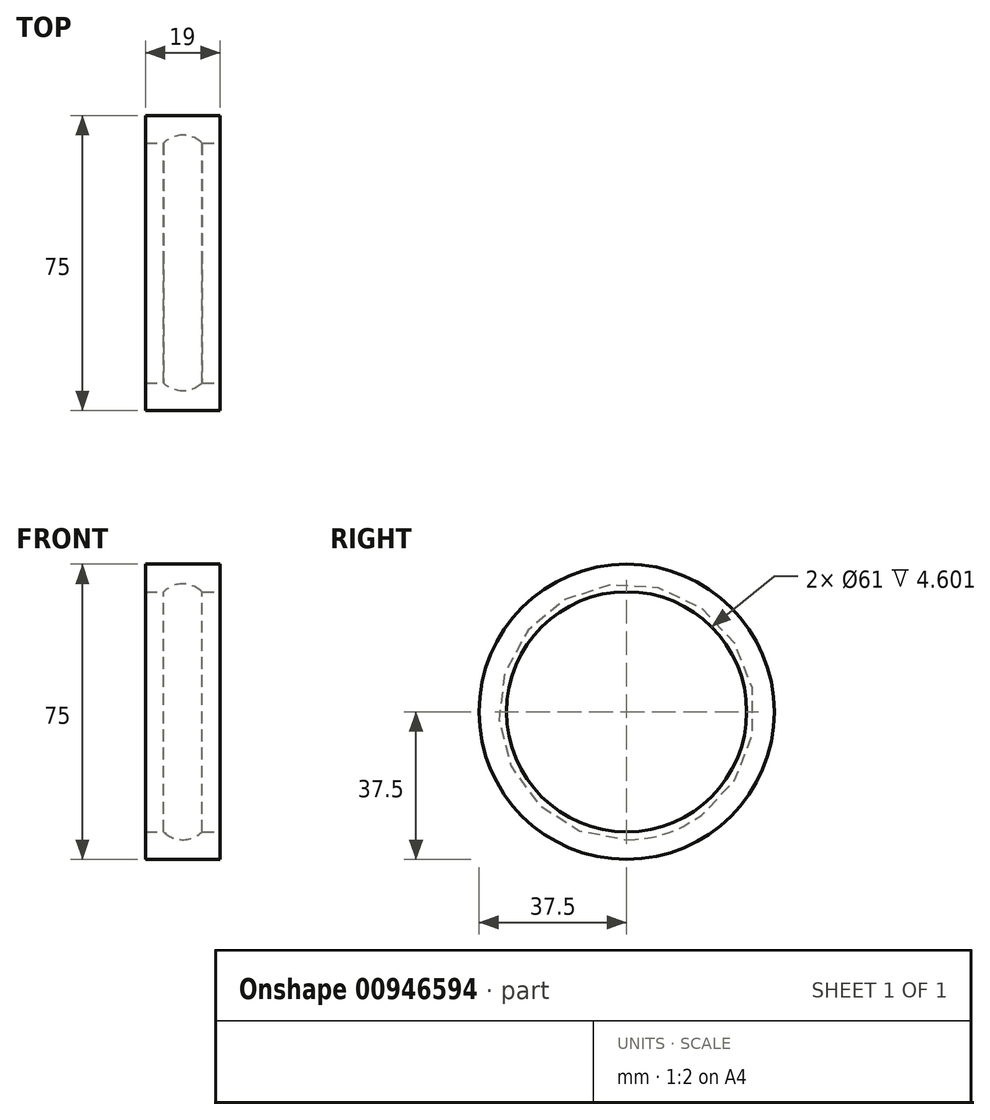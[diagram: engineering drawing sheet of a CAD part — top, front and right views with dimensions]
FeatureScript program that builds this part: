
annotation { "Feature Type Name" : "Feature", "Feature Type Description" : "" }
export const myFeature = defineFeature(function(context is Context, id is Id, definition is map)
    precondition{}
    {
        {
            var Q0;
            Q0=qCreatedBy(makeId("Front.planeOp"),FACE);
            var sketch = newSketch(context, id + "F0", { "sketchPlane" : qUnion([Q0])});
            skLineSegment(sketch, "E0.bottom", {"start": v(-9.5, 0) * mm, "end": v(9.5, 0) * mm});
            skLineSegment(sketch, "E0.top", {"start": v(-9.5, 7) * mm, "end": v(-4.9, 7) * mm});
            skLineSegment(sketch, "E0.left", {"start": v(-9.5, 0) * mm, "end": v(-9.5, 7) * mm});
            skLineSegment(sketch, "E0.right", {"start": v(9.5, 0) * mm, "end": v(9.5, 7) * mm});
            skArc(sketch, "E1", {"start": v(-4.9, 7) * mm, "mid": v(0, 5) * mm, "end": v(4.9, 7) * mm});
            skPoint(sketch, "E1.centerSnap0", {"position": v(0, 7) * mm});
            skLineSegment(sketch, "E2.trimOffspring", {"start": v(4.9, 7) * mm, "end": v(9.5, 7) * mm});
            skLineSegment(sketch, "E3", {"start": v(0, 37.5) * mm, "end": v(-16.98, 37.5) * mm, "construction": true});
            skSolve(sketch);
        }
        {
            var Q0;
            Q0 = qSketchRegion(id + "F0", true);
            var Q1;
            Q1=sQuery(id+"F0.wireOp",EDGE,"E3");
            revolve(context, id + "F1", {"surfaceOperationType" : NewSurfaceOperationType.NEW, "entities" : qUnion([Q0]), "axis" : qUnion([Q1]), "revolveType" : RevolveType.FULL});
        }
    });
